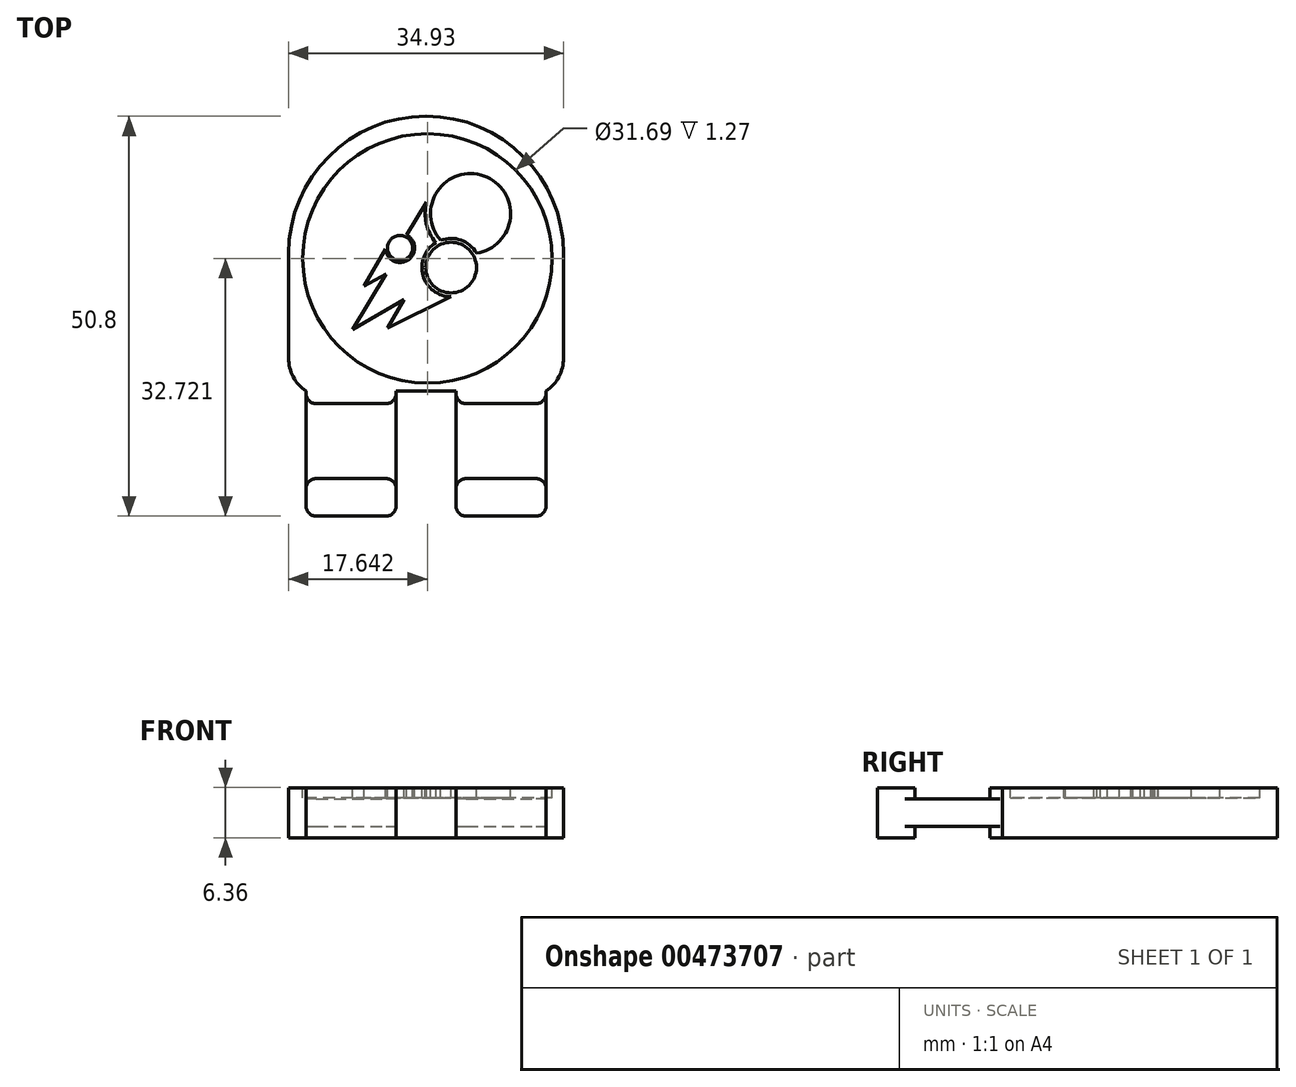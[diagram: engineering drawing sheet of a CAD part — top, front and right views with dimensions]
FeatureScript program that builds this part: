
annotation { "Feature Type Name" : "Feature", "Feature Type Description" : "" }
export const myFeature = defineFeature(function(context is Context, id is Id, definition is map)
    precondition{}
    {
        {
            var Q0;
            Q0=qCreatedBy(makeId("Top.planeOp"),FACE);
            var sketch = newSketch(context, id + "F0", { "sketchPlane" : qUnion([Q0])});
            skLineSegment(sketch, "E0.bottom", {"start": v(-17.15, 21.98) * mm, "end": v(17.78, 21.98) * mm});
            skLineSegment(sketch, "E0.top", {"start": v(-14.92, -28.82) * mm, "end": v(-3.5, -28.82) * mm});
            skLineSegment(sketch, "E0.left", {"start": v(-17.15, 21.98) * mm, "end": v(-17.15, -12.94) * mm});
            skLineSegment(sketch, "E0.right", {"start": v(17.78, 21.98) * mm, "end": v(17.78, -12.94) * mm});
            skPoint(sketch, "E0.middle", {"position": v(0, 0) * mm});
            skLineSegment(sketch, "E1", {"start": v(-17.15, -12.94) * mm, "end": v(-14.92, -12.94) * mm});
            skLineSegment(sketch, "E2", {"start": v(-14.92, -12.94) * mm, "end": v(-14.92, -28.82) * mm});
            skLineSegment(sketch, "E3", {"start": v(-3.5, -28.82) * mm, "end": v(-3.5, -12.94) * mm});
            skLineSegment(sketch, "E4", {"start": v(-3.5, -12.94) * mm, "end": v(4.13, -12.94) * mm});
            skLineSegment(sketch, "E5", {"start": v(4.13, -12.94) * mm, "end": v(4.13, -28.82) * mm});
            skLineSegment(sketch, "E6", {"start": v(17.78, -12.94) * mm, "end": v(15.56, -12.94) * mm});
            skLineSegment(sketch, "E7", {"start": v(15.56, -12.94) * mm, "end": v(15.56, -28.82) * mm});
            skLineSegment(sketch, "E8.trimOffspring", {"start": v(4.13, -28.82) * mm, "end": v(15.56, -28.82) * mm});
            skSolve(sketch);
        }
        {
            var Q0;
            Q0=qSketchRegion(id+"F0",true);
            extrude(context, id + "F1", {"entities" : qUnion([Q0]), "endBound" : BoundingType.SYMMETRIC, "depth" : 6.35 * mm});
        }
        {
            var Q0;
            Q0=qCreatedBy(makeId("Right.planeOp"),FACE);
            var sketch = newSketch(context, id + "F2", { "sketchPlane" : qUnion([Q0])});
            skLineSegment(sketch, "E9", {"start": v(-14.53, -1.73) * mm, "end": v(-24.05, -1.73) * mm});
            skLineSegment(sketch, "E10", {"start": v(-24.05, -1.73) * mm, "end": v(-24.05, -3.18) * mm});
            skLineSegment(sketch, "E11", {"start": v(-24.05, -3.18) * mm, "end": v(-14.53, -3.18) * mm});
            skLineSegment(sketch, "E12", {"start": v(-14.53, 1.73) * mm, "end": v(-24.05, 1.73) * mm});
            skLineSegment(sketch, "E13", {"start": v(-24.05, 1.73) * mm, "end": v(-24.05, 3.18) * mm});
            skLineSegment(sketch, "E14", {"start": v(-24.05, 3.18) * mm, "end": v(-14.53, 3.18) * mm});
            skLineSegment(sketch, "E15", {"start": v(-14.53, 1.73) * mm, "end": v(-14.53, 3.18) * mm});
            skLineSegment(sketch, "E16", {"start": v(-14.53, -3.18) * mm, "end": v(-14.53, -1.73) * mm});
            skSolve(sketch);
        }
        {
            var Q0;
            Q0=qSketchRegion(id+"F2",true);
            extrude(context, id + "F3", {"entities" : qUnion([Q0]), "operationType" : NewBodyOperationType.REMOVE, "endBound" : BoundingType.SYMMETRIC, "oppositeDirection" : true, "depth" : 50.8 * mm});
        }
        {
            var Q0;
            {var subQ0=sQuery(id+"F0.wireOp",EDGE,"E1");var subQ1=sQuery(id+"F0.wireOp",EDGE,"E0.left");var subQ2=sQuery(id+"F0.wireOp",EDGE,"E0.right");var subQ3=sQuery(id+"F0.wireOp",EDGE,"E0.bottom");var subQ4=sQuery(id+"F0.wireOp",EDGE,"E6");var subQ5=sQuery(id+"F0.wireOp",EDGE,"E4");Q0=makeQuery(id+"F3.boolean.opBoolean","SPLIT",FACE,{"disambiguationData":[TD([makeQuery(id+"F1.opExtrude","SWEPT_FACE",FACE,{"disambiguationData":[OSD([subQ3])]})])],"derivedFrom":makeQuery(id+"F1.opExtrude","CAP_FACE",FACE,{"disambiguationData":[OSD([subQ3,sQuery(id+"F0.wireOp",EDGE,"E0.top"),subQ1,subQ2,subQ0,sQuery(id+"F0.wireOp",EDGE,"E2"),sQuery(id+"F0.wireOp",EDGE,"E3"),subQ5,sQuery(id+"F0.wireOp",EDGE,"E5"),subQ4,sQuery(id+"F0.wireOp",EDGE,"E7"),sQuery(id+"F0.wireOp",EDGE,"E8.trimOffspring")])],"isStart":false})});}
            var sketch = newSketch(context, id + "F4", { "sketchPlane" : qUnion([Q0])});
            skCircle(sketch, "E17", {"center": v(0.5, 3.9) * mm, "radius": 15.84 * mm});
            skPoint(sketch, "E18", {"position": v(-17.15, 4.52) * mm});
            skArc(sketch, "E19", {"start": v(6.72, 4.58) * mm, "mid": v(7.69, 14.39) * mm, "end": v(2.18, 6.22) * mm});
            skCircle(sketch, "E20", {"center": v(3.5, 2.75) * mm, "radius": 3.22 * mm});
            skCircle(sketch, "E21", {"center": v(-2.98, 5.24) * mm, "radius": 1.6 * mm});
            skArc(sketch, "E22", {"start": v(0.4, 11.1) * mm, "mid": v(0.35, 8.36) * mm, "end": v(1.55, 5.9) * mm});
            skArc(sketch, "E23", {"start": v(6.72, 4.58) * mm, "mid": v(4.75, 6.24) * mm, "end": v(2.18, 6.22) * mm});
            skArc(sketch, "E24", {"start": v(-4.83, 5.12) * mm, "mid": v(-1.97, 3.7) * mm, "end": v(-2.14, 6.89) * mm});
            skLineSegment(sketch, "E25", {"start": v(-7.55, 0.42) * mm, "end": v(-4.83, 5.12) * mm});
            skLineSegment(sketch, "E26", {"start": v(-7.55, 0.42) * mm, "end": v(-4.76, 1.95) * mm});
            skLineSegment(sketch, "E27", {"start": v(-4.76, 1.95) * mm, "end": v(-9.03, -5.11) * mm});
            skLineSegment(sketch, "E28", {"start": v(-9.03, -5.11) * mm, "end": v(-2.48, -1.32) * mm});
            skLineSegment(sketch, "E29", {"start": v(-2.48, -1.32) * mm, "end": v(-4.55, -4.91) * mm});
            skLineSegment(sketch, "E30", {"start": v(-4.55, -4.91) * mm, "end": v(3.48, -0.96) * mm});
            skLineSegment(sketch, "E31.trimOffspring", {"start": v(-2.14, 6.89) * mm, "end": v(0.4, 11.1) * mm});
            skArc(sketch, "E32.trimOffspring", {"start": v(1.55, 5.9) * mm, "mid": v(-0.07, 1.75) * mm, "end": v(3.48, -0.96) * mm});
            skLineSegment(sketch, "E33", {"start": v(-17.15, 21.98) * mm, "end": v(17.78, 21.98) * mm});
            skLineSegment(sketch, "E34", {"start": v(17.78, 21.98) * mm, "end": v(17.78, -12.94) * mm});
            skLineSegment(sketch, "E35", {"start": v(17.78, -12.94) * mm, "end": v(-17.15, -12.94) * mm});
            skLineSegment(sketch, "E36", {"start": v(-17.15, 21.98) * mm, "end": v(-17.15, -12.94) * mm});
            skSolve(sketch);
        }
        {
            var Q0;
            Q0=makeQuery(id+"F4.imprint","IMPRINT",FACE,{"disambiguationData":[TD([[makeQuery(id+"F4.imprint","IMPRINT",EDGE,{"derivedFrom":sQuery(id+"F4.wireOp",EDGE,"E17")}),1.0]])]});
            extrude(context, id + "F5", {"entities" : qUnion([Q0]), "operationType" : NewBodyOperationType.REMOVE, "oppositeDirection" : true, "depth" : 1.27 * mm});
        }
        {
            var Q0;
            Q0=makeQuery(id+"F1.opExtrude","SWEPT_EDGE",EDGE,{"disambiguationData":[OSD([sQuery(id+"F0.wireOp",EDGE,"E0.bottom"),sQuery(id+"F0.wireOp",EDGE,"E0.right")])]});
            var Q1;
            Q1=makeQuery(id+"F1.opExtrude","SWEPT_EDGE",EDGE,{"disambiguationData":[OSD([sQuery(id+"F0.wireOp",EDGE,"E0.left"),sQuery(id+"F0.wireOp",EDGE,"E1")])]});
            var Q2;
            Q2=makeQuery(id+"F1.opExtrude","SWEPT_EDGE",EDGE,{"disambiguationData":[OSD([sQuery(id+"F0.wireOp",EDGE,"E0.right"),sQuery(id+"F0.wireOp",EDGE,"E6")])]});
            var Q3;
            Q3=makeQuery(id+"F1.opExtrude","SWEPT_EDGE",EDGE,{"disambiguationData":[OSD([sQuery(id+"F0.wireOp",EDGE,"E0.bottom"),sQuery(id+"F0.wireOp",EDGE,"E0.left")])]});
            fillet(context, id + "F6", {"entities" : qUnion([Q0, Q1, Q2, Q3]), "radius" : 5.08 * mm, "tangentPropagation" : true, "allowEdgeOverflow" : false});
        }
        {
            var Q0;
            {var subQ0=makeQuery(id+"F3.opExtrude","SWEPT_FACE",FACE,{"disambiguationData":[OSD([sQuery(id+"F2.wireOp",EDGE,"x62yvcTG-1TIA-uCk9-cSXU-WGpYtcgAMLtR")])]});var subQ1=makeQuery(id+"F3.opExtrude","SWEPT_FACE",FACE,{"disambiguationData":[OSD([sQuery(id+"F2.wireOp",EDGE,"bjkGccF4-ztdF-G65M-RJ6u-XlurXhTa0Hjr")])]});Q0=makeQuery(id+"F6.opFillet","BLEND_EDGE",EDGE,{"blendedFrom":[makeQuery(id+"F3.boolean.opBoolean","INTERSECT",EDGE,{"disambiguationData":[topologyDisambiguationEdgeConnected([makeQuery(id+"F1.opExtrude","SWEPT_FACE",FACE,{"disambiguationData":[OSD([sQuery(id+"F0.wireOp",EDGE,"E0.right")])]})])],"derivedFrom":[subQ0,subQ1]}),makeQuery(id+"F1.opExtrude","SWEPT_FACE",FACE,{"disambiguationData":[OSD([sQuery(id+"F0.wireOp",EDGE,"E7")])]})],"blendedInto":[makeQuery(id+"F1.opExtrude","SWEPT_FACE",FACE,{"disambiguationData":[OSD([sQuery(id+"F0.wireOp",EDGE,"E7")])]})]});}
            var Q1;
            {var subQ0=makeQuery(id+"F3.opExtrude","SWEPT_FACE",FACE,{"disambiguationData":[OSD([sQuery(id+"F2.wireOp",EDGE,"x62yvcTG-1TIA-uCk9-cSXU-WGpYtcgAMLtR")])]});var subQ1=makeQuery(id+"F3.opExtrude","SWEPT_FACE",FACE,{"disambiguationData":[OSD([sQuery(id+"F2.wireOp",EDGE,"bjkGccF4-ztdF-G65M-RJ6u-XlurXhTa0Hjr")])]});Q1=makeQuery(id+"F6.opFillet","BLEND_EDGE",EDGE,{"blendedFrom":[makeQuery(id+"F3.boolean.opBoolean","INTERSECT",EDGE,{"disambiguationData":[topologyDisambiguationEdgeConnected([makeQuery(id+"F1.opExtrude","SWEPT_FACE",FACE,{"disambiguationData":[OSD([sQuery(id+"F0.wireOp",EDGE,"E0.left")])]})])],"derivedFrom":[subQ0,subQ1]}),makeQuery(id+"F1.opExtrude","SWEPT_FACE",FACE,{"disambiguationData":[OSD([sQuery(id+"F0.wireOp",EDGE,"E2")])]})],"blendedInto":[makeQuery(id+"F1.opExtrude","SWEPT_FACE",FACE,{"disambiguationData":[OSD([sQuery(id+"F0.wireOp",EDGE,"E2")])]})]});}
            var Q2;
            Q2=makeQuery(id+"F3.boolean.opBoolean","INTERSECT",EDGE,{"derivedFrom":[makeQuery(id+"F1.opExtrude","SWEPT_FACE",FACE,{"disambiguationData":[OSD([sQuery(id+"F0.wireOp",EDGE,"E2")])]}),makeQuery(id+"F3.opExtrude","SWEPT_FACE",FACE,{"disambiguationData":[OSD([sQuery(id+"F2.wireOp",EDGE,"E15")])]})]});
            var Q3;
            Q3=makeQuery(id+"F3.boolean.opBoolean","INTERSECT",EDGE,{"derivedFrom":[makeQuery(id+"F1.opExtrude","SWEPT_FACE",FACE,{"disambiguationData":[OSD([sQuery(id+"F0.wireOp",EDGE,"E3")])]}),makeQuery(id+"F3.opExtrude","SWEPT_FACE",FACE,{"disambiguationData":[OSD([sQuery(id+"F2.wireOp",EDGE,"E15")])]})]});
            var Q4;
            Q4=makeQuery(id+"F3.boolean.opBoolean","INTERSECT",EDGE,{"derivedFrom":[makeQuery(id+"F1.opExtrude","SWEPT_FACE",FACE,{"disambiguationData":[OSD([sQuery(id+"F0.wireOp",EDGE,"E7")])]}),makeQuery(id+"F3.opExtrude","SWEPT_FACE",FACE,{"disambiguationData":[OSD([sQuery(id+"F2.wireOp",EDGE,"E15")])]})]});
            var Q5;
            Q5=makeQuery(id+"F3.boolean.opBoolean","INTERSECT",EDGE,{"derivedFrom":[makeQuery(id+"F1.opExtrude","SWEPT_FACE",FACE,{"disambiguationData":[OSD([sQuery(id+"F0.wireOp",EDGE,"E5")])]}),makeQuery(id+"F3.opExtrude","SWEPT_FACE",FACE,{"disambiguationData":[OSD([sQuery(id+"F2.wireOp",EDGE,"E15")])]})]});
            var Q6;
            Q6=makeQuery(id+"F3.boolean.opBoolean","INTERSECT",EDGE,{"derivedFrom":[makeQuery(id+"F1.opExtrude","SWEPT_FACE",FACE,{"disambiguationData":[OSD([sQuery(id+"F0.wireOp",EDGE,"E7")])]}),makeQuery(id+"F3.opExtrude","SWEPT_FACE",FACE,{"disambiguationData":[OSD([sQuery(id+"F2.wireOp",EDGE,"E16")])]})]});
            var Q7;
            Q7=makeQuery(id+"F3.boolean.opBoolean","INTERSECT",EDGE,{"derivedFrom":[makeQuery(id+"F1.opExtrude","SWEPT_FACE",FACE,{"disambiguationData":[OSD([sQuery(id+"F0.wireOp",EDGE,"E5")])]}),makeQuery(id+"F3.opExtrude","SWEPT_FACE",FACE,{"disambiguationData":[OSD([sQuery(id+"F2.wireOp",EDGE,"E16")])]})]});
            var Q8;
            Q8=makeQuery(id+"F3.boolean.opBoolean","INTERSECT",EDGE,{"derivedFrom":[makeQuery(id+"F1.opExtrude","SWEPT_FACE",FACE,{"disambiguationData":[OSD([sQuery(id+"F0.wireOp",EDGE,"E2")])]}),makeQuery(id+"F3.opExtrude","SWEPT_FACE",FACE,{"disambiguationData":[OSD([sQuery(id+"F2.wireOp",EDGE,"E16")])]})]});
            var Q9;
            Q9=makeQuery(id+"F3.boolean.opBoolean","INTERSECT",EDGE,{"derivedFrom":[makeQuery(id+"F1.opExtrude","SWEPT_FACE",FACE,{"disambiguationData":[OSD([sQuery(id+"F0.wireOp",EDGE,"E3")])]}),makeQuery(id+"F3.opExtrude","SWEPT_FACE",FACE,{"disambiguationData":[OSD([sQuery(id+"F2.wireOp",EDGE,"E16")])]})]});
            var Q10;
            Q10=makeQuery(id+"F3.boolean.opBoolean","INTERSECT",EDGE,{"derivedFrom":[makeQuery(id+"F1.opExtrude","SWEPT_FACE",FACE,{"disambiguationData":[OSD([sQuery(id+"F0.wireOp",EDGE,"E3")])]}),makeQuery(id+"F3.opExtrude","SWEPT_FACE",FACE,{"disambiguationData":[OSD([sQuery(id+"F2.wireOp",EDGE,"E10")])]})]});
            var Q11;
            Q11=makeQuery(id+"F3.boolean.opBoolean","INTERSECT",EDGE,{"derivedFrom":[makeQuery(id+"F1.opExtrude","SWEPT_FACE",FACE,{"disambiguationData":[OSD([sQuery(id+"F0.wireOp",EDGE,"E3")])]}),makeQuery(id+"F3.opExtrude","SWEPT_FACE",FACE,{"disambiguationData":[OSD([sQuery(id+"F2.wireOp",EDGE,"E13")])]})]});
            var Q12;
            Q12=makeQuery(id+"F3.boolean.opBoolean","INTERSECT",EDGE,{"derivedFrom":[makeQuery(id+"F1.opExtrude","SWEPT_FACE",FACE,{"disambiguationData":[OSD([sQuery(id+"F0.wireOp",EDGE,"E7")])]}),makeQuery(id+"F3.opExtrude","SWEPT_FACE",FACE,{"disambiguationData":[OSD([sQuery(id+"F2.wireOp",EDGE,"E10")])]})]});
            var Q13;
            Q13=makeQuery(id+"F3.boolean.opBoolean","INTERSECT",EDGE,{"derivedFrom":[makeQuery(id+"F1.opExtrude","SWEPT_FACE",FACE,{"disambiguationData":[OSD([sQuery(id+"F0.wireOp",EDGE,"E7")])]}),makeQuery(id+"F3.opExtrude","SWEPT_FACE",FACE,{"disambiguationData":[OSD([sQuery(id+"F2.wireOp",EDGE,"E13")])]})]});
            var Q14;
            Q14=makeQuery(id+"F1.opExtrude","SWEPT_EDGE",EDGE,{"disambiguationData":[OSD([sQuery(id+"F0.wireOp",EDGE,"E7"),sQuery(id+"F0.wireOp",EDGE,"E8.trimOffspring")])]});
            var Q15;
            Q15=makeQuery(id+"F1.opExtrude","SWEPT_EDGE",EDGE,{"disambiguationData":[OSD([sQuery(id+"F0.wireOp",EDGE,"E5"),sQuery(id+"F0.wireOp",EDGE,"E8.trimOffspring")])]});
            var Q16;
            Q16=makeQuery(id+"F1.opExtrude","SWEPT_EDGE",EDGE,{"disambiguationData":[OSD([sQuery(id+"F0.wireOp",EDGE,"E0.top"),sQuery(id+"F0.wireOp",EDGE,"E3")])]});
            var Q17;
            Q17=makeQuery(id+"F1.opExtrude","SWEPT_EDGE",EDGE,{"disambiguationData":[OSD([sQuery(id+"F0.wireOp",EDGE,"E0.top"),sQuery(id+"F0.wireOp",EDGE,"E2")])]});
            var Q18;
            Q18=makeQuery(id+"F3.boolean.opBoolean","INTERSECT",EDGE,{"derivedFrom":[makeQuery(id+"F1.opExtrude","SWEPT_FACE",FACE,{"disambiguationData":[OSD([sQuery(id+"F0.wireOp",EDGE,"E2")])]}),makeQuery(id+"F3.opExtrude","SWEPT_FACE",FACE,{"disambiguationData":[OSD([sQuery(id+"F2.wireOp",EDGE,"E13")])]})]});
            var Q19;
            Q19=makeQuery(id+"F3.boolean.opBoolean","INTERSECT",EDGE,{"derivedFrom":[makeQuery(id+"F1.opExtrude","SWEPT_FACE",FACE,{"disambiguationData":[OSD([sQuery(id+"F0.wireOp",EDGE,"E2")])]}),makeQuery(id+"F3.opExtrude","SWEPT_FACE",FACE,{"disambiguationData":[OSD([sQuery(id+"F2.wireOp",EDGE,"E10")])]})]});
            var Q20;
            Q20=makeQuery(id+"F3.boolean.opBoolean","INTERSECT",EDGE,{"derivedFrom":[makeQuery(id+"F1.opExtrude","SWEPT_FACE",FACE,{"disambiguationData":[OSD([sQuery(id+"F0.wireOp",EDGE,"E5")])]}),makeQuery(id+"F3.opExtrude","SWEPT_FACE",FACE,{"disambiguationData":[OSD([sQuery(id+"F2.wireOp",EDGE,"E13")])]})]});
            var Q21;
            Q21=makeQuery(id+"F3.boolean.opBoolean","INTERSECT",EDGE,{"derivedFrom":[makeQuery(id+"F1.opExtrude","SWEPT_FACE",FACE,{"disambiguationData":[OSD([sQuery(id+"F0.wireOp",EDGE,"E5")])]}),makeQuery(id+"F3.opExtrude","SWEPT_FACE",FACE,{"disambiguationData":[OSD([sQuery(id+"F2.wireOp",EDGE,"E10")])]})]});
            fillet(context, id + "F7", {"entities" : qUnion([Q0, Q1, Q2, Q3, Q4, Q5, Q6, Q7, Q8, Q9, Q10, Q11, Q12, Q13, Q14, Q15, Q16, Q17, Q18, Q19, Q20, Q21]), "radius" : 1.27 * mm, "tangentPropagation" : true, "allowEdgeOverflow" : false});
        }
        {
            var Q0;
            {var subQ0=sQuery(id+"F0.wireOp",EDGE,"E7");var subQ2=sQuery(id+"F0.wireOp",EDGE,"E5");var subQ4=sQuery(id+"F0.wireOp",EDGE,"E4");var subQ6=sQuery(id+"F0.wireOp",EDGE,"E6");var subQ7=sQuery(id+"F0.wireOp",EDGE,"E3");var subQ8=sQuery(id+"F0.wireOp",EDGE,"E2");var subQ9=sQuery(id+"F0.wireOp",EDGE,"E1");var subQ10=sQuery(id+"F0.wireOp",EDGE,"E0.right");var subQ11=sQuery(id+"F0.wireOp",EDGE,"E0.left");var subQ12=sQuery(id+"F0.wireOp",EDGE,"E0.bottom");var subQ13=makeQuery(id+"F1.opExtrude","CAP_FACE",FACE,{"disambiguationData":[OSD([subQ12,sQuery(id+"F0.wireOp",EDGE,"E0.top"),subQ11,subQ10,subQ9,subQ8,subQ7,subQ4,subQ2,subQ6,subQ0,sQuery(id+"F0.wireOp",EDGE,"E8.trimOffspring")])],"isStart":false});var subQ19=makeQuery(id+"F1.opExtrude","SWEPT_FACE",FACE,{"disambiguationData":[OSD([subQ12])]});Q0=makeQuery(id+"F5.boolean.opBoolean","SPLIT",FACE,{"disambiguationData":[TD([subQ19])],"derivedFrom":makeQuery(id+"F3.boolean.opBoolean","SPLIT",FACE,{"disambiguationData":[TD([subQ19])],"derivedFrom":subQ13})});}
            var sketch = newSketch(context, id + "F8", { "sketchPlane" : qUnion([Q0])});
            skCircle(sketch, "E37", {"center": v(0.32, 4.52) * mm, "radius": 17.46 * mm});
            skLineSegment(sketch, "E38", {"start": v(-17.15, 4.08) * mm, "end": v(-17.15, 21.98) * mm});
            skLineSegment(sketch, "E39", {"start": v(-17.15, 21.98) * mm, "end": v(17.78, 21.98) * mm});
            skLineSegment(sketch, "E40", {"start": v(17.78, 21.98) * mm, "end": v(17.78, 4.08) * mm});
            skSolve(sketch);
        }
        {
            var Q0;
            {var subQ0=sQuery(id+"F8.wireOp",EDGE,"E38");var subQ25=sQuery(id+"F8.wireOp",EDGE,"E39");var subQ26=makeQuery(id+"F8.imprint","INTERSECT",VERTEX,{"derivedFrom":[subQ0,subQ25]});Q0=makeQuery(id+"F8.imprint","IMPRINT",FACE,{"disambiguationData":[TD([[makeQuery(id+"F8.imprint","IMPRINT",EDGE,{"disambiguationData":[TD([[subQ26,1.0]])],"derivedFrom":subQ0}),-1.0]])]});}
            var Q1;
            {var subQ0=sQuery(id+"F8.wireOp",EDGE,"E39");var subQ25=sQuery(id+"F8.wireOp",EDGE,"E40");var subQ26=makeQuery(id+"F8.imprint","INTERSECT",VERTEX,{"derivedFrom":[subQ0,subQ25]});Q1=makeQuery(id+"F8.imprint","IMPRINT",FACE,{"disambiguationData":[TD([[makeQuery(id+"F8.imprint","IMPRINT",EDGE,{"disambiguationData":[TD([[subQ26,1.0]])],"derivedFrom":subQ0}),-1.0]])]});}
            var Q2;
            {var subQ0=sQuery(id+"F8.wireOp",EDGE,"E39");var subQ1=sQuery(id+"F8.wireOp",EDGE,"E37");var subQ2=makeQuery(id+"F8.imprint","INTERSECT",VERTEX,{"derivedFrom":[subQ1,subQ0]});Q2=makeQuery(id+"F8.imprint","IMPRINT",FACE,{"disambiguationData":[TD([[makeQuery(id+"F8.imprint","IMPRINT",EDGE,{"disambiguationData":[TD([[subQ2,1.0]])],"derivedFrom":subQ1}),-1.0]])]});}
            var Q3;
            {var subQ0=sQuery(id+"F8.wireOp",EDGE,"E39");var subQ1=sQuery(id+"F8.wireOp",EDGE,"E37");var subQ2=makeQuery(id+"F8.imprint","INTERSECT",VERTEX,{"derivedFrom":[subQ1,subQ0]});Q3=makeQuery(id+"F8.imprint","IMPRINT",FACE,{"disambiguationData":[TD([[makeQuery(id+"F8.imprint","IMPRINT",EDGE,{"disambiguationData":[TD([[subQ2,-1.0]])],"derivedFrom":subQ1}),-1.0]])]});}
            extrude(context, id + "F9", {"entities" : qUnion([Q0, Q1, Q2, Q3]), "operationType" : NewBodyOperationType.REMOVE, "oppositeDirection" : true, "depth" : 25.4 * mm});
        }
    });
